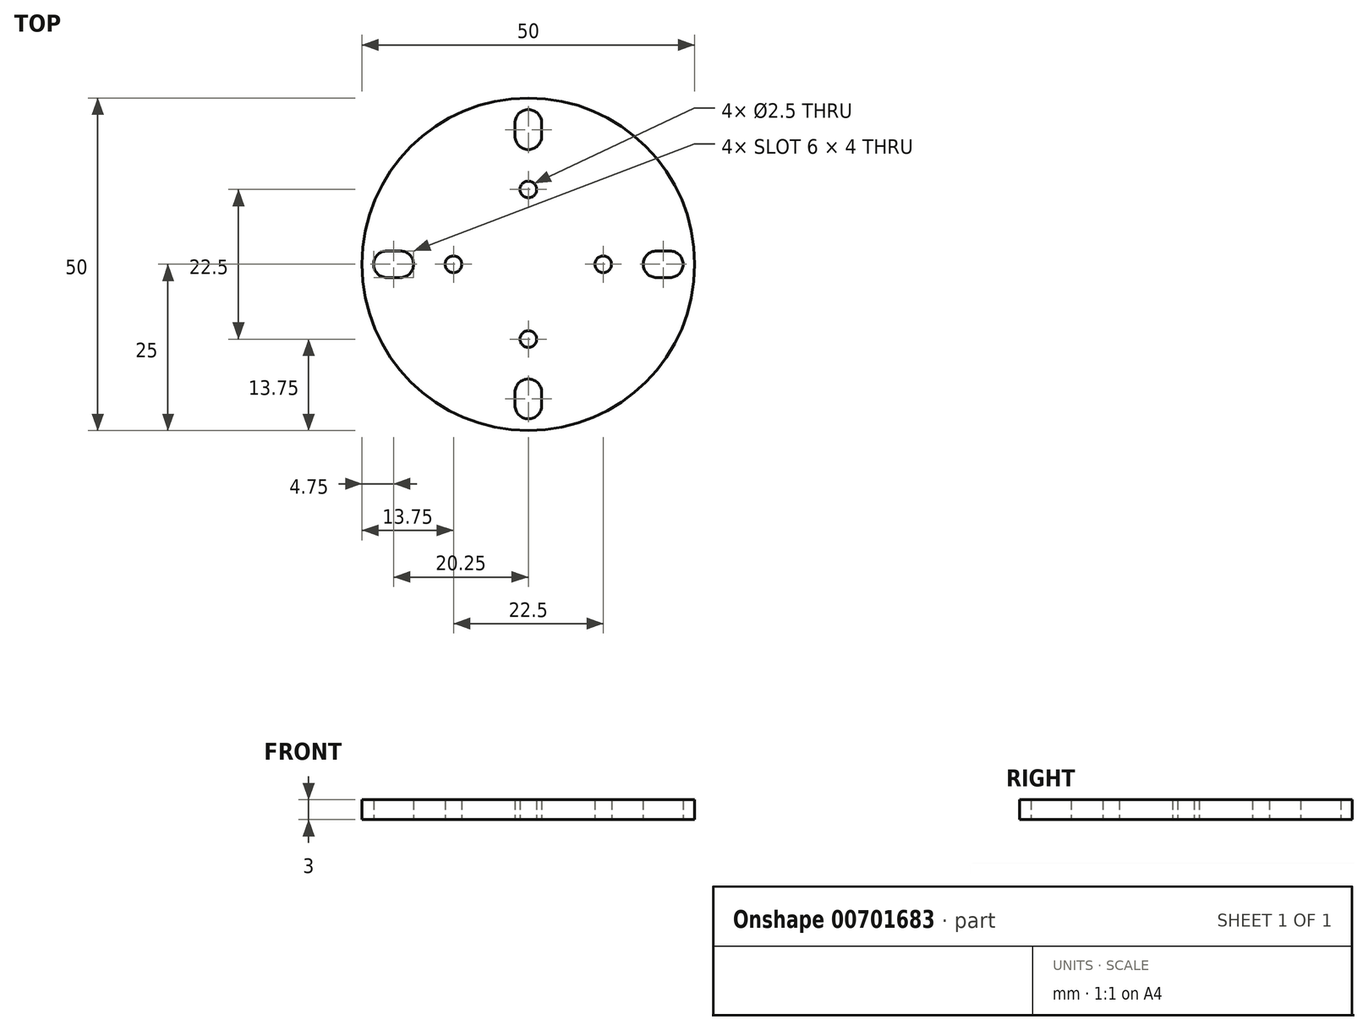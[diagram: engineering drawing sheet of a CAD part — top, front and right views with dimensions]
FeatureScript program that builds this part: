
annotation { "Feature Type Name" : "Feature", "Feature Type Description" : "" }
export const myFeature = defineFeature(function(context is Context, id is Id, definition is map)
    precondition{}
    {
        {
            var Q0;
            Q0=qCreatedBy(makeId("Top.planeOp"),FACE);
            var sketch = newSketch(context, id + "F0", { "sketchPlane" : qUnion([Q0])});
            skCircle(sketch, "E0", {"center": v(0, 0) * mm, "radius": 25 * mm});
            skCircle(sketch, "E1", {"center": v(-11.25, 0) * mm, "radius": 1.25 * mm});
            skCircle(sketch, "E2.MirrorC", {"center": v(11.25, 0) * mm, "radius": 1.25 * mm});
            skLineSegment(sketch, "E3", {"start": v(0, 0) * mm, "end": v(-21.79, 21.79) * mm, "construction": true});
            skCircle(sketch, "E4.MirrorC", {"center": v(0, 11.25) * mm, "radius": 1.25 * mm});
            skCircle(sketch, "E5.MirrorC", {"center": v(0, -11.25) * mm, "radius": 1.25 * mm});
            skArc(sketch, "E6", {"start": v(-21.25, -2) * mm, "mid": v(-23.25, 0) * mm, "end": v(-21.25, 2) * mm});
            skArc(sketch, "E7", {"start": v(-19.25, -2) * mm, "mid": v(-17.25, 0) * mm, "end": v(-19.25, 2) * mm});
            skPoint(sketch, "E8", {"position": v(-20.25, 0) * mm});
            skLineSegment(sketch, "E9", {"start": v(-19.25, 2) * mm, "end": v(-21.25, 2) * mm});
            skLineSegment(sketch, "E10", {"start": v(-19.25, -2) * mm, "end": v(-21.25, -2) * mm});
            skArc(sketch, "E11.MirrorCS", {"start": v(21.25, -2) * mm, "mid": v(23.25, 0) * mm, "end": v(21.25, 2) * mm});
            skLineSegment(sketch, "E12.MirrorCS", {"start": v(19.25, 2) * mm, "end": v(21.25, 2) * mm});
            skArc(sketch, "E13.MirrorCS", {"start": v(19.25, -2) * mm, "mid": v(17.25, 0) * mm, "end": v(19.25, 2) * mm});
            skLineSegment(sketch, "E14.MirrorCS", {"start": v(19.25, -2) * mm, "end": v(21.25, -2) * mm});
            skLineSegment(sketch, "E15.MirrorCS", {"start": v(-2, -19.25) * mm, "end": v(-2, -21.25) * mm});
            skArc(sketch, "E16.MirrorCS", {"start": v(2, -21.25) * mm, "mid": v(0, -23.25) * mm, "end": v(-2, -21.25) * mm});
            skLineSegment(sketch, "E17.MirrorCS", {"start": v(2, -19.25) * mm, "end": v(2, -21.25) * mm});
            skArc(sketch, "E18.MirrorCS", {"start": v(2, -19.25) * mm, "mid": v(0, -17.25) * mm, "end": v(-2, -19.25) * mm});
            skArc(sketch, "E19.MirrorCS", {"start": v(2, 19.25) * mm, "mid": v(0, 17.25) * mm, "end": v(-2, 19.25) * mm});
            skLineSegment(sketch, "E20.MirrorCS", {"start": v(2, 19.25) * mm, "end": v(2, 21.25) * mm});
            skArc(sketch, "E21.MirrorCS", {"start": v(2, 21.25) * mm, "mid": v(0, 23.25) * mm, "end": v(-2, 21.25) * mm});
            skLineSegment(sketch, "E22.MirrorCS", {"start": v(-2, 19.25) * mm, "end": v(-2, 21.25) * mm});
            skSolve(sketch);
        }
        {
            var Q0;
            Q0=makeQuery(id+"F0.imprint","IMPRINT",FACE,{"disambiguationData":[TD([[makeQuery(id+"F0.imprint","IMPRINT",EDGE,{"derivedFrom":sQuery(id+"F0.wireOp",EDGE,"E0")}),1.0]])]});
            extrude(context, id + "F1", {"entities" : qUnion([Q0]), "depth" : 3 * mm, "offsetDistance" : 25 * mm});
        }
    });
